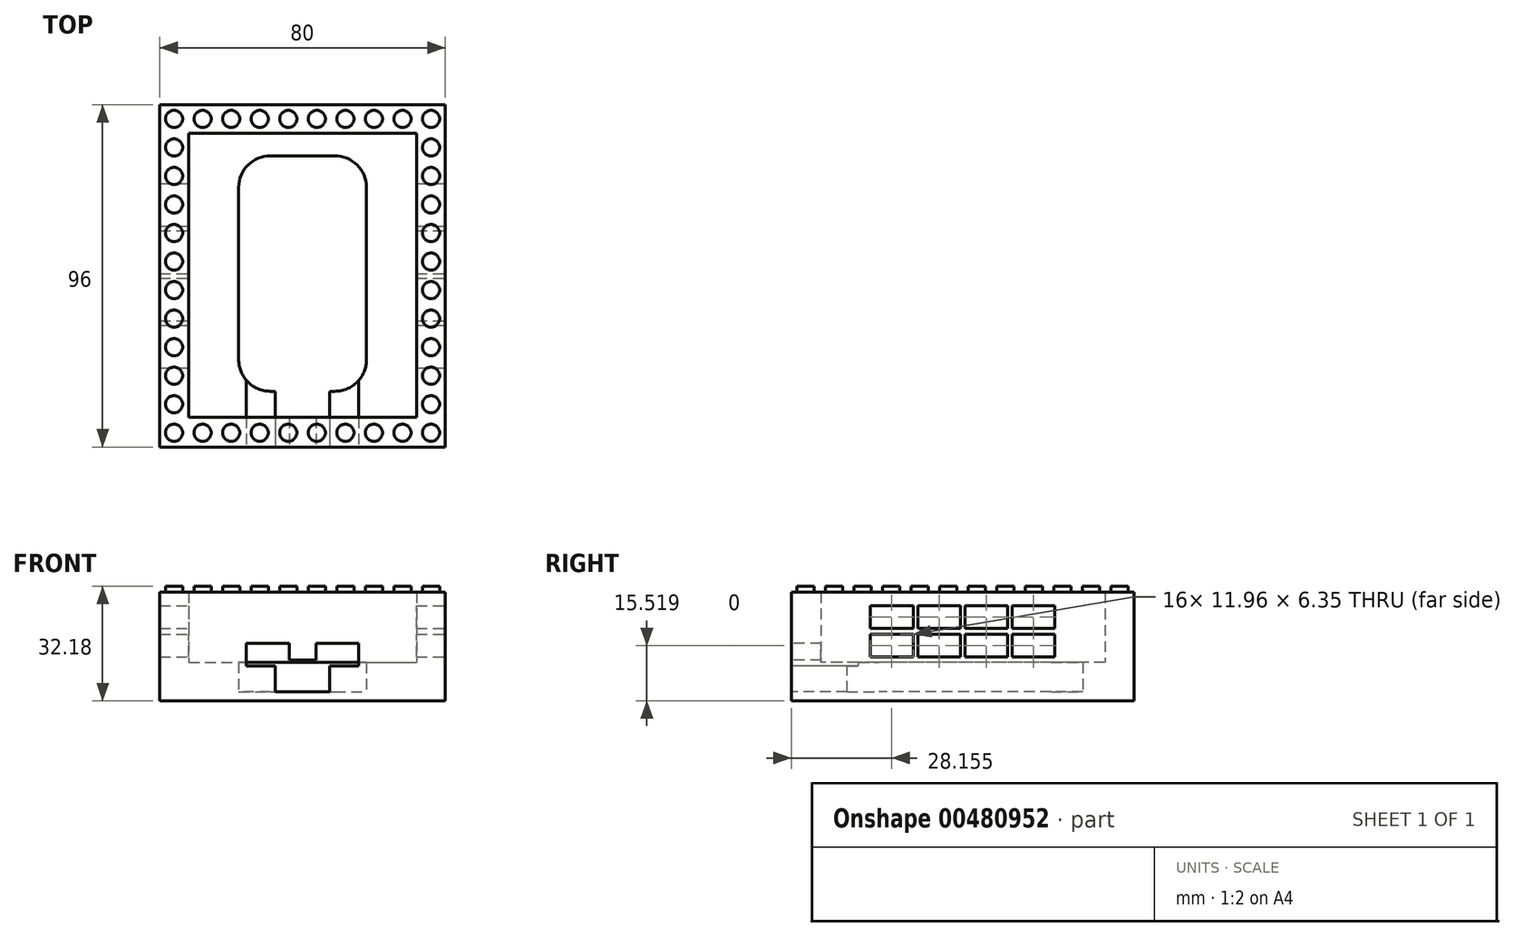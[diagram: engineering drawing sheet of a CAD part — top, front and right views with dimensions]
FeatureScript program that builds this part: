
annotation { "Feature Type Name" : "Feature", "Feature Type Description" : "" }
export const myFeature = defineFeature(function(context is Context, id is Id, definition is map)
    precondition{}
    {
        {
            var Q0;
            Q0=qCreatedBy(makeId("Top.planeOp"),FACE);
            var sketch = newSketch(context, id + "F0", { "sketchPlane" : qUnion([Q0])});
            skLineSegment(sketch, "E0.bottom", {"start": v(0, 0) * mm, "end": v(63.83, 0) * mm});
            skLineSegment(sketch, "E0.top", {"start": v(0, -79.62) * mm, "end": v(63.83, -79.62) * mm});
            skLineSegment(sketch, "E0.left", {"start": v(0, 0) * mm, "end": v(0, -79.62) * mm});
            skLineSegment(sketch, "E0.right", {"start": v(63.83, 0) * mm, "end": v(63.83, -79.62) * mm});
            skLineSegment(sketch, "E1.0", {"start": v(-8.08, 8.08) * mm, "end": v(71.92, 8.08) * mm});
            skLineSegment(sketch, "E1.1", {"start": v(-8.08, 8.08) * mm, "end": v(-8.08, -87.92) * mm});
            skLineSegment(sketch, "E1.2", {"start": v(-8.08, -87.92) * mm, "end": v(71.92, -87.92) * mm});
            skLineSegment(sketch, "E1.3", {"start": v(71.92, 8.08) * mm, "end": v(71.92, -87.92) * mm});
            skSolve(sketch);
        }
        {
            var Q0;
            Q0=makeQuery(id+"F0.imprint","IMPRINT",FACE,{"disambiguationData":[TD([[makeQuery(id+"F0.imprint","IMPRINT",EDGE,{"derivedFrom":sQuery(id+"F0.wireOp",EDGE,"E0.bottom")}),1.0]])]});
            extrude(context, id + "F1", {"entities" : qUnion([Q0]), "depth" : 27.94 * mm});
        }
        {
            var Q0;
            Q0=qCreatedBy(makeId("Top.planeOp"),FACE);
            var sketch = newSketch(context, id + "F2", { "sketchPlane" : qUnion([Q0])});
            skLineSegment(sketch, "E2.0.0", {"start": v(71.92, -87.92) * mm, "end": v(71.92, 8.08) * mm});
            skLineSegment(sketch, "E2.0.1", {"start": v(71.92, 8.08) * mm, "end": v(-8.08, 8.08) * mm});
            skLineSegment(sketch, "E2.0.2", {"start": v(-8.08, 8.08) * mm, "end": v(-8.08, -87.92) * mm});
            skLineSegment(sketch, "E2.0.3", {"start": v(-8.08, -87.92) * mm, "end": v(71.92, -87.92) * mm});
            skLineSegment(sketch, "E3.0", {"start": v(63.83, 0) * mm, "end": v(63.83, -79.62) * mm});
            skLineSegment(sketch, "E4.0", {"start": v(0, -79.62) * mm, "end": v(63.83, -79.62) * mm});
            skLineSegment(sketch, "E5.0", {"start": v(0, 0) * mm, "end": v(0, -79.62) * mm});
            skLineSegment(sketch, "E6.0", {"start": v(0, 0) * mm, "end": v(63.83, 0) * mm});
            skSolve(sketch);
        }
        {
            var Q0;
            Q0=makeQuery(id+"F2.imprint","IMPRINT",FACE,{"disambiguationData":[TD([[makeQuery(id+"F2.imprint","IMPRINT",EDGE,{"derivedFrom":sQuery(id+"F2.wireOp",EDGE,"E2.0.0")}),1.0]])]});
            var Q1;
            Q1=makeQuery(id+"F2.imprint","IMPRINT",FACE,{"disambiguationData":[TD([[makeQuery(id+"F2.imprint","IMPRINT",EDGE,{"derivedFrom":sQuery(id+"F2.wireOp",EDGE,"E3.0")}),-1.0]])]});
            extrude(context, id + "F3", {"entities" : qUnion([Q0, Q1]), "operationType" : NewBodyOperationType.ADD, "oppositeDirection" : true, "depth" : 2.54 * mm});
        }
        {
            var Q0;
            Q0=makeQuery(id+"F3.opExtrude","CAP_FACE",FACE,{"disambiguationData":[OSD([sQuery(id+"F2.wireOp",EDGE,"E2.0.0"),sQuery(id+"F2.wireOp",EDGE,"E2.0.1"),sQuery(id+"F2.wireOp",EDGE,"E2.0.2"),sQuery(id+"F2.wireOp",EDGE,"E2.0.3")])],"isStart":true});
            var sketch = newSketch(context, id + "F4", { "sketchPlane" : qUnion([Q0])});
            skLineSegment(sketch, "E7.bottom", {"start": v(22.9, -6.25) * mm, "end": v(40.94, -6.25) * mm});
            skLineSegment(sketch, "E7.top", {"start": v(22.9, -72.3) * mm, "end": v(28.11, -72.3) * mm});
            skLineSegment(sketch, "E7.left", {"start": v(14.01, -15.14) * mm, "end": v(14.01, -63.4) * mm});
            skLineSegment(sketch, "E7.right", {"start": v(49.83, -15.14) * mm, "end": v(49.83, -63.4) * mm});
            skPoint(sketch, "E8.visualSharp", {"position": v(14.01, -6.25) * mm});
            skArc(sketch, "E8.filletArc", {"start": v(22.9, -6.25) * mm, "mid": v(16.62, -8.86) * mm, "end": v(14.01, -15.14) * mm});
            skPoint(sketch, "E9.visualSharp", {"position": v(49.83, -6.25) * mm});
            skArc(sketch, "E9.filletArc", {"start": v(49.83, -15.14) * mm, "mid": v(47.22, -8.86) * mm, "end": v(40.94, -6.25) * mm});
            skPoint(sketch, "E10.visualSharp", {"position": v(49.83, -72.3) * mm});
            skArc(sketch, "E10.filletArc", {"start": v(40.94, -72.3) * mm, "mid": v(47.22, -69.7) * mm, "end": v(49.83, -63.4) * mm});
            skPoint(sketch, "E11.visualSharp", {"position": v(14.01, -72.3) * mm});
            skArc(sketch, "E11.filletArc", {"start": v(14.01, -63.4) * mm, "mid": v(16.62, -69.7) * mm, "end": v(22.9, -72.3) * mm});
            skLineSegment(sketch, "E12.0.0", {"start": v(0, 0) * mm, "end": v(0, -79.62) * mm});
            skLineSegment(sketch, "E12.0.1", {"start": v(0, -79.62) * mm, "end": v(63.83, -79.62) * mm});
            skLineSegment(sketch, "E12.0.2", {"start": v(63.83, -79.62) * mm, "end": v(63.83, 0) * mm});
            skLineSegment(sketch, "E12.0.3", {"start": v(63.83, 0) * mm, "end": v(0, 0) * mm});
            skLineSegment(sketch, "E13.top", {"start": v(31.92, -73.82) * mm, "end": v(35.73, -73.82) * mm});
            skLineSegment(sketch, "E13.right", {"start": v(35.73, -72.3) * mm, "end": v(35.73, -73.82) * mm});
            skLineSegment(sketch, "E14.top", {"start": v(32.3, -73.82) * mm, "end": v(28.11, -73.82) * mm});
            skLineSegment(sketch, "E14.right", {"start": v(28.11, -72.3) * mm, "end": v(28.11, -73.82) * mm});
            skLineSegment(sketch, "E15.trimOffspring", {"start": v(35.73, -72.3) * mm, "end": v(40.94, -72.3) * mm});
            skPoint(sketch, "E14.bottom.start.orphan", {"position": v(31.92, -72.3) * mm});
            skSolve(sketch);
        }
        {
            var Q0;
            Q0=makeQuery(id+"F4.imprint","IMPRINT",FACE,{"disambiguationData":[TD([[makeQuery(id+"F4.imprint","IMPRINT",EDGE,{"derivedFrom":sQuery(id+"F4.wireOp",EDGE,"E7.bottom")}),1.0]])]});
            extrude(context, id + "F5", {"entities" : qUnion([Q0]), "operationType" : NewBodyOperationType.ADD, "depth" : 8.25 * mm});
        }
        {
            var Q0;
            Q0=makeQuery(id+"F3.boolean.opBoolean","MERGE",FACE,{"derivedFrom":[makeQuery(id+"F1.opExtrude","SWEPT_FACE",FACE,{"disambiguationData":[OSD([sQuery(id+"F0.wireOp",EDGE,"E1.2")])]}),makeQuery(id+"F3.opExtrude","SWEPT_FACE",FACE,{"disambiguationData":[OSD([sQuery(id+"F2.wireOp",EDGE,"E2.0.3")])]})]});
            var sketch = newSketch(context, id + "F6", { "sketchPlane" : qUnion([Q0])});
            skLineSegment(sketch, "E16.0.0", {"start": v(-8.08, 27.94) * mm, "end": v(-8.08, -2.54) * mm});
            skLineSegment(sketch, "E16.0.1", {"start": v(-8.08, -2.54) * mm, "end": v(71.92, -2.54) * mm});
            skLineSegment(sketch, "E16.0.2", {"start": v(71.92, -2.54) * mm, "end": v(71.92, 27.94) * mm});
            skLineSegment(sketch, "E16.0.3", {"start": v(71.92, 27.94) * mm, "end": v(-8.08, 27.94) * mm});
            skPoint(sketch, "E17.firstSnap0", {"position": v(31.92, -2.54) * mm});
            skLineSegment(sketch, "E17.bottom", {"start": v(31.92, 8.9) * mm, "end": v(39.54, 8.9) * mm});
            skLineSegment(sketch, "E17.top", {"start": v(31.92, 0) * mm, "end": v(39.54, 0) * mm});
            skLineSegment(sketch, "E17.left", {"start": v(31.92, 8.9) * mm, "end": v(31.92, 0) * mm});
            skLineSegment(sketch, "E17.right", {"start": v(39.54, 8.9) * mm, "end": v(39.54, 0) * mm});
            skLineSegment(sketch, "E18.bottom", {"start": v(31.92, 0) * mm, "end": v(24.3, 0) * mm});
            skLineSegment(sketch, "E18.top", {"start": v(31.92, 8.89) * mm, "end": v(24.3, 8.89) * mm});
            skLineSegment(sketch, "E18.left", {"start": v(31.92, 0) * mm, "end": v(31.92, 8.89) * mm});
            skLineSegment(sketch, "E18.right", {"start": v(24.3, 0) * mm, "end": v(24.3, 8.89) * mm});
            skLineSegment(sketch, "E19.bottom", {"start": v(24.3, 0) * mm, "end": v(37, 0) * mm});
            skSolve(sketch);
        }
        {
            var Q0;
            Q0=makeQuery(id+"F6.imprint","IMPRINT",FACE,{"disambiguationData":[TD([[makeQuery(id+"F6.imprint","IMPRINT",EDGE,{"derivedFrom":sQuery(id+"F6.wireOp",EDGE,"E17.bottom")}),-1.0]])]});
            var Q1;
            Q1=makeQuery(id+"F6.imprint","IMPRINT",FACE,{"disambiguationData":[TD([[makeQuery(id+"F6.imprint","IMPRINT",EDGE,{"derivedFrom":sQuery(id+"F6.wireOp",EDGE,"E18.bottom")}),-1.0]])]});
            var Q2;
            Q2=makeQuery(id+"F6.imprint","IMPRINT",FACE,{"disambiguationData":[TD([[makeQuery(id+"F6.imprint","IMPRINT",EDGE,{"derivedFrom":sQuery(id+"F6.wireOp",EDGE,"E18.top")}),1.0]])]});
            var Q3;
            Q3=makeQuery(id+"F6.imprint","IMPRINT",FACE,{"disambiguationData":[TD([[makeQuery(id+"F6.imprint","IMPRINT",EDGE,{"derivedFrom":sQuery(id+"F6.wireOp",EDGE,"E19.top")}),1.0]])]});
            extrude(context, id + "F7", {"entities" : qUnion([Q0, Q1, Q2, Q3]), "operationType" : NewBodyOperationType.REMOVE, "oppositeDirection" : true, "depth" : 25.4 * mm});
        }
        {
            var Q0;
            Q0=makeQuery(id+"F3.boolean.opBoolean","MERGE",FACE,{"derivedFrom":[makeQuery(id+"F1.opExtrude","SWEPT_FACE",FACE,{"disambiguationData":[OSD([sQuery(id+"F0.wireOp",EDGE,"E1.2")])]}),makeQuery(id+"F3.opExtrude","SWEPT_FACE",FACE,{"disambiguationData":[OSD([sQuery(id+"F2.wireOp",EDGE,"E2.0.3")])]})]});
            var sketch = newSketch(context, id + "F8", { "sketchPlane" : qUnion([Q0])});
            skLineSegment(sketch, "E20.bottom", {"start": v(16.18, 13.59) * mm, "end": v(28.14, 13.59) * mm});
            skLineSegment(sketch, "E20.top", {"start": v(16.18, 7.24) * mm, "end": v(28.14, 7.24) * mm});
            skLineSegment(sketch, "E20.left", {"start": v(16.18, 13.59) * mm, "end": v(16.18, 7.24) * mm});
            skLineSegment(sketch, "E20.right", {"start": v(28.14, 13.59) * mm, "end": v(28.14, 7.24) * mm});
            skLineSegment(sketch, "E21.0.0", {"start": v(-8.08, 27.94) * mm, "end": v(-8.08, -2.54) * mm});
            skLineSegment(sketch, "E21.0.1", {"start": v(-8.08, -2.54) * mm, "end": v(71.92, -2.54) * mm});
            skLineSegment(sketch, "E21.0.2", {"start": v(71.92, -2.54) * mm, "end": v(71.92, 27.94) * mm});
            skLineSegment(sketch, "E21.0.3", {"start": v(71.92, 27.94) * mm, "end": v(-8.08, 27.94) * mm});
            skLineSegment(sketch, "E22", {"start": v(31.92, 27.94) * mm, "end": v(31.92, -2.54) * mm});
            skLineSegment(sketch, "E23.MirrorCS", {"start": v(47.65, 13.59) * mm, "end": v(35.69, 13.59) * mm});
            skLineSegment(sketch, "E24.MirrorCS", {"start": v(47.65, 13.59) * mm, "end": v(47.65, 7.24) * mm});
            skLineSegment(sketch, "E25.MirrorCS", {"start": v(47.65, 7.24) * mm, "end": v(35.69, 7.24) * mm});
            skLineSegment(sketch, "E26.MirrorCS", {"start": v(35.69, 13.59) * mm, "end": v(35.69, 7.24) * mm});
            skSolve(sketch);
        }
        {
            var Q0;
            Q0=makeQuery(id+"F8.imprint","IMPRINT",FACE,{"disambiguationData":[TD([[makeQuery(id+"F8.imprint","IMPRINT",EDGE,{"derivedFrom":sQuery(id+"F8.wireOp",EDGE,"E20.bottom")}),-1.0]])]});
            var Q1;
            Q1=makeQuery(id+"F8.imprint","IMPRINT",FACE,{"disambiguationData":[TD([[makeQuery(id+"F8.imprint","IMPRINT",EDGE,{"derivedFrom":sQuery(id+"F8.wireOp",EDGE,"E23.MirrorCS")}),1.0]])]});
            extrude(context, id + "F9", {"entities" : qUnion([Q0, Q1]), "operationType" : NewBodyOperationType.REMOVE, "oppositeDirection" : true, "depth" : 19.05 * mm});
        }
        {
            var Q0;
            Q0=makeQuery(id+"F3.boolean.opBoolean","MERGE",FACE,{"derivedFrom":[makeQuery(id+"F1.opExtrude","SWEPT_FACE",FACE,{"disambiguationData":[OSD([sQuery(id+"F0.wireOp",EDGE,"E1.3")])]}),makeQuery(id+"F3.opExtrude","SWEPT_FACE",FACE,{"disambiguationData":[OSD([sQuery(id+"F2.wireOp",EDGE,"E2.0.0")])]})]});
            var sketch = newSketch(context, id + "F10", { "sketchPlane" : qUnion([Q0])});
            skLineSegment(sketch, "E27.bottom", {"start": v(-39.28, 24.13) * mm, "end": v(-27.32, 24.13) * mm});
            skLineSegment(sketch, "E27.top", {"start": v(-39.28, 17.78) * mm, "end": v(-27.32, 17.78) * mm});
            skLineSegment(sketch, "E27.left", {"start": v(-39.28, 24.13) * mm, "end": v(-39.28, 17.78) * mm});
            skLineSegment(sketch, "E27.right", {"start": v(-27.32, 24.13) * mm, "end": v(-27.32, 17.78) * mm});
            skLineSegment(sketch, "E28.bottom", {"start": v(-26.05, 24.13) * mm, "end": v(-14.08, 24.13) * mm});
            skLineSegment(sketch, "E28.top", {"start": v(-26.05, 17.78) * mm, "end": v(-14.08, 17.78) * mm});
            skLineSegment(sketch, "E28.left", {"start": v(-26.05, 24.13) * mm, "end": v(-26.05, 17.78) * mm});
            skLineSegment(sketch, "E28.right", {"start": v(-14.08, 24.13) * mm, "end": v(-14.08, 17.78) * mm});
            skLineSegment(sketch, "E29.bottom", {"start": v(-40.55, 17.78) * mm, "end": v(-52.51, 17.78) * mm});
            skLineSegment(sketch, "E29.top", {"start": v(-40.55, 24.13) * mm, "end": v(-52.51, 24.13) * mm});
            skLineSegment(sketch, "E29.left", {"start": v(-40.55, 17.78) * mm, "end": v(-40.55, 24.13) * mm});
            skLineSegment(sketch, "E29.right", {"start": v(-52.51, 17.78) * mm, "end": v(-52.51, 24.13) * mm});
            skLineSegment(sketch, "E30.bottom", {"start": v(-53.78, 17.78) * mm, "end": v(-65.75, 17.78) * mm});
            skLineSegment(sketch, "E30.top", {"start": v(-53.78, 24.13) * mm, "end": v(-65.75, 24.13) * mm});
            skLineSegment(sketch, "E30.left", {"start": v(-53.78, 17.78) * mm, "end": v(-53.78, 24.13) * mm});
            skLineSegment(sketch, "E30.right", {"start": v(-65.75, 17.78) * mm, "end": v(-65.75, 24.13) * mm});
            skLineSegment(sketch, "E31", {"start": v(-39.92, -2.54) * mm, "end": v(-39.92, 27.94) * mm});
            skLineSegment(sketch, "E32.0.1.0", {"start": v(-26.05, 16.15) * mm, "end": v(-26.05, 9.8) * mm});
            skLineSegment(sketch, "E32.0.1.1", {"start": v(-26.05, 16.15) * mm, "end": v(-14.08, 16.15) * mm});
            skLineSegment(sketch, "E32.0.1.2", {"start": v(-26.05, 9.8) * mm, "end": v(-14.08, 9.8) * mm});
            skLineSegment(sketch, "E32.0.1.3", {"start": v(-14.08, 16.15) * mm, "end": v(-14.08, 9.8) * mm});
            skLineSegment(sketch, "E32.0.1.4", {"start": v(-27.32, 16.15) * mm, "end": v(-27.32, 9.8) * mm});
            skLineSegment(sketch, "E32.0.1.5", {"start": v(-39.28, 16.15) * mm, "end": v(-27.32, 16.15) * mm});
            skLineSegment(sketch, "E32.0.1.6", {"start": v(-39.28, 9.8) * mm, "end": v(-27.32, 9.8) * mm});
            skLineSegment(sketch, "E32.0.1.7", {"start": v(-39.28, 16.15) * mm, "end": v(-39.28, 9.8) * mm});
            skLineSegment(sketch, "E32.0.1.8", {"start": v(-40.55, 9.8) * mm, "end": v(-40.55, 16.15) * mm});
            skLineSegment(sketch, "E32.0.1.9", {"start": v(-40.55, 16.15) * mm, "end": v(-52.51, 16.15) * mm});
            skLineSegment(sketch, "E32.0.1.10", {"start": v(-40.55, 9.8) * mm, "end": v(-52.51, 9.8) * mm});
            skLineSegment(sketch, "E32.0.1.11", {"start": v(-52.51, 9.8) * mm, "end": v(-52.51, 16.15) * mm});
            skLineSegment(sketch, "E32.0.1.12", {"start": v(-53.78, 9.8) * mm, "end": v(-53.78, 16.15) * mm});
            skLineSegment(sketch, "E32.0.1.13", {"start": v(-53.78, 16.15) * mm, "end": v(-65.75, 16.15) * mm});
            skLineSegment(sketch, "E32.0.1.14", {"start": v(-53.78, 9.8) * mm, "end": v(-65.75, 9.8) * mm});
            skLineSegment(sketch, "E32.0.1.15", {"start": v(-65.75, 9.8) * mm, "end": v(-65.75, 16.15) * mm});
            skLineSegment(sketch, "E32.direction1", {"start": v(-26.05, 17.78) * mm, "end": v(-0.54, 17.78) * mm, "construction": true});
            skLineSegment(sketch, "E32.direction2", {"start": v(-26.05, 17.78) * mm, "end": v(-26.05, 9.8) * mm, "construction": true});
            skSolve(sketch);
        }
        {
            var Q0;
            Q0 = qSketchRegion(id + "F10", true);
            extrude(context, id + "F11", {"entities" : qUnion([Q0]), "operationType" : NewBodyOperationType.REMOVE, "oppositeDirection" : true, "depth" : 127 * mm});
        }
        {
            var Q0;
            Q0=makeQuery(id+"F1.opExtrude","CAP_FACE",FACE,{"disambiguationData":[OSD([sQuery(id+"F0.wireOp",EDGE,"E0.bottom"),sQuery(id+"F0.wireOp",EDGE,"E0.top"),sQuery(id+"F0.wireOp",EDGE,"E0.left"),sQuery(id+"F0.wireOp",EDGE,"E0.right"),sQuery(id+"F0.wireOp",EDGE,"E1.0"),sQuery(id+"F0.wireOp",EDGE,"E1.1"),sQuery(id+"F0.wireOp",EDGE,"E1.2"),sQuery(id+"F0.wireOp",EDGE,"E1.3")])],"isStart":false});
            var sketch = newSketch(context, id + "F12", { "sketchPlane" : qUnion([Q0])});
            skCircle(sketch, "E33", {"center": v(-4.08, -83.92) * mm, "radius": 2.4 * mm});
            skCircle(sketch, "E34.1.0.0", {"center": v(3.92, -83.92) * mm, "radius": 2.4 * mm});
            skCircle(sketch, "E34.2.0.0", {"center": v(11.92, -83.92) * mm, "radius": 2.4 * mm});
            skCircle(sketch, "E34.3.0.0", {"center": v(19.92, -83.92) * mm, "radius": 2.4 * mm});
            skCircle(sketch, "E34.4.0.0", {"center": v(27.92, -83.92) * mm, "radius": 2.4 * mm});
            skCircle(sketch, "E34.5.0.0", {"center": v(35.92, -83.92) * mm, "radius": 2.4 * mm});
            skCircle(sketch, "E34.6.0.0", {"center": v(43.92, -83.92) * mm, "radius": 2.4 * mm});
            skCircle(sketch, "E34.7.0.0", {"center": v(51.92, -83.92) * mm, "radius": 2.4 * mm});
            skCircle(sketch, "E34.8.0.0", {"center": v(59.92, -83.92) * mm, "radius": 2.4 * mm});
            skCircle(sketch, "E34.9.0.0", {"center": v(67.92, -83.92) * mm, "radius": 2.4 * mm});
            skLineSegment(sketch, "E34.direction1", {"start": v(-4.08, -83.92) * mm, "end": v(3.92, -83.92) * mm, "construction": true});
            skCircle(sketch, "E35.0.1.0", {"center": v(-4.08, -75.92) * mm, "radius": 2.4 * mm});
            skCircle(sketch, "E35.0.2.0", {"center": v(-4.08, -67.92) * mm, "radius": 2.4 * mm});
            skCircle(sketch, "E35.0.3.0", {"center": v(-4.08, -59.92) * mm, "radius": 2.4 * mm});
            skCircle(sketch, "E35.0.4.0", {"center": v(-4.08, -51.92) * mm, "radius": 2.4 * mm});
            skCircle(sketch, "E35.0.5.0", {"center": v(-4.08, -43.92) * mm, "radius": 2.4 * mm});
            skCircle(sketch, "E35.0.6.0", {"center": v(-4.08, -35.92) * mm, "radius": 2.4 * mm});
            skCircle(sketch, "E35.0.7.0", {"center": v(-4.08, -27.92) * mm, "radius": 2.4 * mm});
            skCircle(sketch, "E35.0.8.0", {"center": v(-4.08, -19.92) * mm, "radius": 2.4 * mm});
            skCircle(sketch, "E35.0.9.0", {"center": v(-4.08, -11.92) * mm, "radius": 2.4 * mm});
            skCircle(sketch, "E35.0.10.0", {"center": v(-4.08, -3.92) * mm, "radius": 2.4 * mm});
            skCircle(sketch, "E35.0.11.0", {"center": v(-4.08, 4.08) * mm, "radius": 2.4 * mm});
            skLineSegment(sketch, "E35.direction1", {"start": v(-4.08, -83.92) * mm, "end": v(21.32, -83.92) * mm, "construction": true});
            skLineSegment(sketch, "E35.direction2", {"start": v(-4.08, -83.92) * mm, "end": v(-4.08, -75.92) * mm, "construction": true});
            skCircle(sketch, "E36.1.0.0", {"center": v(3.92, 4.08) * mm, "radius": 2.4 * mm});
            skCircle(sketch, "E36.2.0.0", {"center": v(11.92, 4.08) * mm, "radius": 2.4 * mm});
            skCircle(sketch, "E36.3.0.0", {"center": v(19.92, 4.08) * mm, "radius": 2.4 * mm});
            skCircle(sketch, "E36.4.0.0", {"center": v(27.92, 4.08) * mm, "radius": 2.4 * mm});
            skCircle(sketch, "E36.5.0.0", {"center": v(35.92, 4.08) * mm, "radius": 2.4 * mm});
            skCircle(sketch, "E36.6.0.0", {"center": v(43.92, 4.08) * mm, "radius": 2.4 * mm});
            skCircle(sketch, "E36.7.0.0", {"center": v(51.92, 4.08) * mm, "radius": 2.4 * mm});
            skCircle(sketch, "E36.8.0.0", {"center": v(59.92, 4.08) * mm, "radius": 2.4 * mm});
            skCircle(sketch, "E36.9.0.0", {"center": v(67.92, 4.08) * mm, "radius": 2.4 * mm});
            skLineSegment(sketch, "E36.direction1", {"start": v(-4.08, 4.08) * mm, "end": v(3.92, 4.08) * mm, "construction": true});
            skCircle(sketch, "E37.0.1.0", {"center": v(67.92, -3.92) * mm, "radius": 2.4 * mm});
            skCircle(sketch, "E37.0.2.0", {"center": v(67.92, -11.92) * mm, "radius": 2.4 * mm});
            skCircle(sketch, "E37.0.3.0", {"center": v(67.92, -19.92) * mm, "radius": 2.4 * mm});
            skCircle(sketch, "E37.0.4.0", {"center": v(67.92, -27.92) * mm, "radius": 2.4 * mm});
            skCircle(sketch, "E37.0.5.0", {"center": v(67.92, -35.92) * mm, "radius": 2.4 * mm});
            skCircle(sketch, "E37.0.6.0", {"center": v(67.92, -43.92) * mm, "radius": 2.4 * mm});
            skCircle(sketch, "E37.0.7.0", {"center": v(67.92, -51.92) * mm, "radius": 2.4 * mm});
            skCircle(sketch, "E37.0.8.0", {"center": v(67.92, -59.92) * mm, "radius": 2.4 * mm});
            skCircle(sketch, "E37.0.9.0", {"center": v(67.92, -67.92) * mm, "radius": 2.4 * mm});
            skCircle(sketch, "E37.0.10.0", {"center": v(67.92, -75.92) * mm, "radius": 2.4 * mm});
            skLineSegment(sketch, "E37.direction1", {"start": v(67.92, 4.08) * mm, "end": v(93.32, 4.08) * mm, "construction": true});
            skLineSegment(sketch, "E37.direction2", {"start": v(67.92, 4.08) * mm, "end": v(67.92, -3.92) * mm, "construction": true});
            skCircle(sketch, "E38", {"center": v(-2.9, -109.78) * mm, "radius": 2.4 * mm});
            skCircle(sketch, "E39.1.0.0", {"center": v(5.1, -109.78) * mm, "radius": 2.4 * mm});
            skCircle(sketch, "E39.2.0.0", {"center": v(13.1, -109.78) * mm, "radius": 2.4 * mm});
            skCircle(sketch, "E39.3.0.0", {"center": v(21.1, -109.78) * mm, "radius": 2.4 * mm});
            skSolve(sketch);
        }
        {
            var Q0;
            Q0=makeQuery(id+"F12.imprint","IMPRINT",FACE,{"disambiguationData":[TD([[makeQuery(id+"F12.imprint","IMPRINT",EDGE,{"derivedFrom":sQuery(id+"F12.wireOp",EDGE,"E33")}),1.0]])]});
            var Q1;
            Q1=makeQuery(id+"F12.imprint","IMPRINT",FACE,{"disambiguationData":[TD([[makeQuery(id+"F12.imprint","IMPRINT",EDGE,{"derivedFrom":sQuery(id+"F12.wireOp",EDGE,"E34.1.0.0")}),1.0]])]});
            var Q2;
            Q2=makeQuery(id+"F12.imprint","IMPRINT",FACE,{"disambiguationData":[TD([[makeQuery(id+"F12.imprint","IMPRINT",EDGE,{"derivedFrom":sQuery(id+"F12.wireOp",EDGE,"E34.2.0.0")}),1.0]])]});
            var Q3;
            Q3=makeQuery(id+"F12.imprint","IMPRINT",FACE,{"disambiguationData":[TD([[makeQuery(id+"F12.imprint","IMPRINT",EDGE,{"derivedFrom":sQuery(id+"F12.wireOp",EDGE,"E34.3.0.0")}),1.0]])]});
            var Q4;
            Q4=makeQuery(id+"F12.imprint","IMPRINT",FACE,{"disambiguationData":[TD([[makeQuery(id+"F12.imprint","IMPRINT",EDGE,{"derivedFrom":sQuery(id+"F12.wireOp",EDGE,"E34.4.0.0")}),1.0]])]});
            var Q5;
            Q5=makeQuery(id+"F12.imprint","IMPRINT",FACE,{"disambiguationData":[TD([[makeQuery(id+"F12.imprint","IMPRINT",EDGE,{"derivedFrom":sQuery(id+"F12.wireOp",EDGE,"E34.5.0.0")}),1.0]])]});
            var Q6;
            Q6=makeQuery(id+"F12.imprint","IMPRINT",FACE,{"disambiguationData":[TD([[makeQuery(id+"F12.imprint","IMPRINT",EDGE,{"derivedFrom":sQuery(id+"F12.wireOp",EDGE,"E34.6.0.0")}),1.0]])]});
            var Q7;
            Q7=makeQuery(id+"F12.imprint","IMPRINT",FACE,{"disambiguationData":[TD([[makeQuery(id+"F12.imprint","IMPRINT",EDGE,{"derivedFrom":sQuery(id+"F12.wireOp",EDGE,"E34.7.0.0")}),1.0]])]});
            var Q8;
            Q8=makeQuery(id+"F12.imprint","IMPRINT",FACE,{"disambiguationData":[TD([[makeQuery(id+"F12.imprint","IMPRINT",EDGE,{"derivedFrom":sQuery(id+"F12.wireOp",EDGE,"E34.9.0.0")}),1.0]])]});
            var Q9;
            Q9=makeQuery(id+"F12.imprint","IMPRINT",FACE,{"disambiguationData":[TD([[makeQuery(id+"F12.imprint","IMPRINT",EDGE,{"derivedFrom":sQuery(id+"F12.wireOp",EDGE,"E34.8.0.0")}),1.0]])]});
            var Q10;
            Q10=makeQuery(id+"F12.imprint","IMPRINT",FACE,{"disambiguationData":[TD([[makeQuery(id+"F12.imprint","IMPRINT",EDGE,{"derivedFrom":sQuery(id+"F12.wireOp",EDGE,"E37.0.10.0")}),1.0]])]});
            var Q11;
            Q11=makeQuery(id+"F12.imprint","IMPRINT",FACE,{"disambiguationData":[TD([[makeQuery(id+"F12.imprint","IMPRINT",EDGE,{"derivedFrom":sQuery(id+"F12.wireOp",EDGE,"E37.0.9.0")}),1.0]])]});
            var Q12;
            Q12=makeQuery(id+"F12.imprint","IMPRINT",FACE,{"disambiguationData":[TD([[makeQuery(id+"F12.imprint","IMPRINT",EDGE,{"derivedFrom":sQuery(id+"F12.wireOp",EDGE,"E37.0.8.0")}),1.0]])]});
            var Q13;
            Q13=makeQuery(id+"F12.imprint","IMPRINT",FACE,{"disambiguationData":[TD([[makeQuery(id+"F12.imprint","IMPRINT",EDGE,{"derivedFrom":sQuery(id+"F12.wireOp",EDGE,"E37.0.7.0")}),1.0]])]});
            var Q14;
            Q14=makeQuery(id+"F12.imprint","IMPRINT",FACE,{"disambiguationData":[TD([[makeQuery(id+"F12.imprint","IMPRINT",EDGE,{"derivedFrom":sQuery(id+"F12.wireOp",EDGE,"E37.0.6.0")}),1.0]])]});
            var Q15;
            Q15=makeQuery(id+"F12.imprint","IMPRINT",FACE,{"disambiguationData":[TD([[makeQuery(id+"F12.imprint","IMPRINT",EDGE,{"derivedFrom":sQuery(id+"F12.wireOp",EDGE,"E37.0.5.0")}),1.0]])]});
            var Q16;
            Q16=makeQuery(id+"F12.imprint","IMPRINT",FACE,{"disambiguationData":[TD([[makeQuery(id+"F12.imprint","IMPRINT",EDGE,{"derivedFrom":sQuery(id+"F12.wireOp",EDGE,"E37.0.4.0")}),1.0]])]});
            var Q17;
            Q17=makeQuery(id+"F12.imprint","IMPRINT",FACE,{"disambiguationData":[TD([[makeQuery(id+"F12.imprint","IMPRINT",EDGE,{"derivedFrom":sQuery(id+"F12.wireOp",EDGE,"E37.0.3.0")}),1.0]])]});
            var Q18;
            Q18=makeQuery(id+"F12.imprint","IMPRINT",FACE,{"disambiguationData":[TD([[makeQuery(id+"F12.imprint","IMPRINT",EDGE,{"derivedFrom":sQuery(id+"F12.wireOp",EDGE,"E37.0.2.0")}),1.0]])]});
            var Q19;
            Q19=makeQuery(id+"F12.imprint","IMPRINT",FACE,{"disambiguationData":[TD([[makeQuery(id+"F12.imprint","IMPRINT",EDGE,{"derivedFrom":sQuery(id+"F12.wireOp",EDGE,"E37.0.1.0")}),1.0]])]});
            var Q20;
            Q20=makeQuery(id+"F12.imprint","IMPRINT",FACE,{"disambiguationData":[TD([[makeQuery(id+"F12.imprint","IMPRINT",EDGE,{"derivedFrom":sQuery(id+"F12.wireOp",EDGE,"E35.0.1.0")}),1.0]])]});
            var Q21;
            Q21=makeQuery(id+"F12.imprint","IMPRINT",FACE,{"disambiguationData":[TD([[makeQuery(id+"F12.imprint","IMPRINT",EDGE,{"derivedFrom":sQuery(id+"F12.wireOp",EDGE,"E35.0.2.0")}),1.0]])]});
            var Q22;
            Q22=makeQuery(id+"F12.imprint","IMPRINT",FACE,{"disambiguationData":[TD([[makeQuery(id+"F12.imprint","IMPRINT",EDGE,{"derivedFrom":sQuery(id+"F12.wireOp",EDGE,"E35.0.3.0")}),1.0]])]});
            var Q23;
            Q23=makeQuery(id+"F12.imprint","IMPRINT",FACE,{"disambiguationData":[TD([[makeQuery(id+"F12.imprint","IMPRINT",EDGE,{"derivedFrom":sQuery(id+"F12.wireOp",EDGE,"E35.0.4.0")}),1.0]])]});
            var Q24;
            Q24=makeQuery(id+"F12.imprint","IMPRINT",FACE,{"disambiguationData":[TD([[makeQuery(id+"F12.imprint","IMPRINT",EDGE,{"derivedFrom":sQuery(id+"F12.wireOp",EDGE,"E35.0.5.0")}),1.0]])]});
            var Q25;
            Q25=makeQuery(id+"F12.imprint","IMPRINT",FACE,{"disambiguationData":[TD([[makeQuery(id+"F12.imprint","IMPRINT",EDGE,{"derivedFrom":sQuery(id+"F12.wireOp",EDGE,"E35.0.6.0")}),1.0]])]});
            var Q26;
            Q26=makeQuery(id+"F12.imprint","IMPRINT",FACE,{"disambiguationData":[TD([[makeQuery(id+"F12.imprint","IMPRINT",EDGE,{"derivedFrom":sQuery(id+"F12.wireOp",EDGE,"E35.0.7.0")}),1.0]])]});
            var Q27;
            Q27=makeQuery(id+"F12.imprint","IMPRINT",FACE,{"disambiguationData":[TD([[makeQuery(id+"F12.imprint","IMPRINT",EDGE,{"derivedFrom":sQuery(id+"F12.wireOp",EDGE,"E35.0.8.0")}),1.0]])]});
            var Q28;
            Q28=makeQuery(id+"F12.imprint","IMPRINT",FACE,{"disambiguationData":[TD([[makeQuery(id+"F12.imprint","IMPRINT",EDGE,{"derivedFrom":sQuery(id+"F12.wireOp",EDGE,"E35.0.9.0")}),1.0]])]});
            var Q29;
            Q29=makeQuery(id+"F12.imprint","IMPRINT",FACE,{"disambiguationData":[TD([[makeQuery(id+"F12.imprint","IMPRINT",EDGE,{"derivedFrom":sQuery(id+"F12.wireOp",EDGE,"E35.0.10.0")}),1.0]])]});
            var Q30;
            Q30=makeQuery(id+"F12.imprint","IMPRINT",FACE,{"disambiguationData":[TD([[makeQuery(id+"F12.imprint","IMPRINT",EDGE,{"derivedFrom":sQuery(id+"F12.wireOp",EDGE,"E35.0.11.0")}),1.0]])]});
            var Q31;
            Q31=makeQuery(id+"F12.imprint","IMPRINT",FACE,{"disambiguationData":[TD([[makeQuery(id+"F12.imprint","IMPRINT",EDGE,{"derivedFrom":sQuery(id+"F12.wireOp",EDGE,"E36.1.0.0")}),1.0]])]});
            var Q32;
            Q32=makeQuery(id+"F12.imprint","IMPRINT",FACE,{"disambiguationData":[TD([[makeQuery(id+"F12.imprint","IMPRINT",EDGE,{"derivedFrom":sQuery(id+"F12.wireOp",EDGE,"E36.2.0.0")}),1.0]])]});
            var Q33;
            Q33=makeQuery(id+"F12.imprint","IMPRINT",FACE,{"disambiguationData":[TD([[makeQuery(id+"F12.imprint","IMPRINT",EDGE,{"derivedFrom":sQuery(id+"F12.wireOp",EDGE,"E36.3.0.0")}),1.0]])]});
            var Q34;
            Q34=makeQuery(id+"F12.imprint","IMPRINT",FACE,{"disambiguationData":[TD([[makeQuery(id+"F12.imprint","IMPRINT",EDGE,{"derivedFrom":sQuery(id+"F12.wireOp",EDGE,"E36.4.0.0")}),1.0]])]});
            var Q35;
            Q35=makeQuery(id+"F12.imprint","IMPRINT",FACE,{"disambiguationData":[TD([[makeQuery(id+"F12.imprint","IMPRINT",EDGE,{"derivedFrom":sQuery(id+"F12.wireOp",EDGE,"E36.8.0.0")}),1.0]])]});
            var Q36;
            Q36=makeQuery(id+"F12.imprint","IMPRINT",FACE,{"disambiguationData":[TD([[makeQuery(id+"F12.imprint","IMPRINT",EDGE,{"derivedFrom":sQuery(id+"F12.wireOp",EDGE,"E36.7.0.0")}),1.0]])]});
            var Q37;
            Q37=makeQuery(id+"F12.imprint","IMPRINT",FACE,{"disambiguationData":[TD([[makeQuery(id+"F12.imprint","IMPRINT",EDGE,{"derivedFrom":sQuery(id+"F12.wireOp",EDGE,"E36.6.0.0")}),1.0]])]});
            var Q38;
            Q38=makeQuery(id+"F12.imprint","IMPRINT",FACE,{"disambiguationData":[TD([[makeQuery(id+"F12.imprint","IMPRINT",EDGE,{"derivedFrom":sQuery(id+"F12.wireOp",EDGE,"E36.5.0.0")}),1.0]])]});
            var Q39;
            Q39=makeQuery(id+"F12.imprint","IMPRINT",FACE,{"disambiguationData":[TD([[makeQuery(id+"F12.imprint","IMPRINT",EDGE,{"derivedFrom":sQuery(id+"F12.wireOp",EDGE,"E36.9.0.0")}),1.0]])]});
            extrude(context, id + "F13", {"entities" : qUnion([Q0, Q1, Q2, Q3, Q4, Q5, Q6, Q7, Q8, Q9, Q10, Q11, Q12, Q13, Q14, Q15, Q16, Q17, Q18, Q19, Q20, Q21, Q22, Q23, Q24, Q25, Q26, Q27, Q28, Q29, Q30, Q31, Q32, Q33, Q34, Q35, Q36, Q37, Q38, Q39]), "operationType" : NewBodyOperationType.ADD, "depth" : 1.7 * mm});
        }
    });
